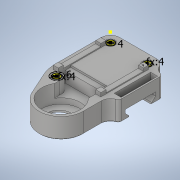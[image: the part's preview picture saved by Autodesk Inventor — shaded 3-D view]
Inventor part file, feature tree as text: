
AUTODESK INVENTOR PART (.ipt)
format: ipt  version: 2021.1 (Build 251245010, 245A)  size: 295,424 bytes
history: mixed  units: in
note: dims shown in document units (in); Inventor stores cm internally (conversion verified against a paired STEP export)
features: extrude x4, direct_edit x3, sketch x3, other x3, chamfer x1, imported_body x1
ambient origin geometry x8: Origin, YZ Plane, XZ Plane, XY Plane, X Axis, Y Axis, Z Axis, Center Point
bodies: Solid1 (imported_parasolid), Body1 (imported_parasolid)
feature tree (15):
  direct_edit  "Direktbearbeitung1"
  direct_edit  "Direktbearbeitung2"
  direct_edit  "Direktbearbeitung3"
  sketch  "Skizze1"  dims[d0=0.1575in d1=0.1575in]
  extrude  "Extrusion1"  Depth=0.1575in
  extrude  "Extrusion2"  Depth=0.1575in
  extrude  "Extrusion3"  Depth=0.2756in TaperAngle=0.0deg
  chamfer  "Fase1"  Distance=0.0197in
  extrude  "Extrusion4"  Depth=0.2756in
  sketch  "Skizze2"  dims[d2=0.1575in d3=0.2362in]
  sketch  "Skizze3"  dims[d4=0.3937in d5=0.0in d6=0.252in d7=0.0in d8=0.0197in d9=0.0197in d10=0.0197in d11=0.0197in d12=0.0in d13=0.0197in d14=0.0787in d15=45.0deg d16=0.2756in d17=0.2362in d18=0.0197in d19=0.0in]
  other  "Löschen1"
  other  "Löschen2"
  other  "Löschen3"
  imported_body  NMx_Import_Brep_tag  [imported B-rep: ~19 faces, bbox_mm=[18.0, 11.0, 51.0]]
